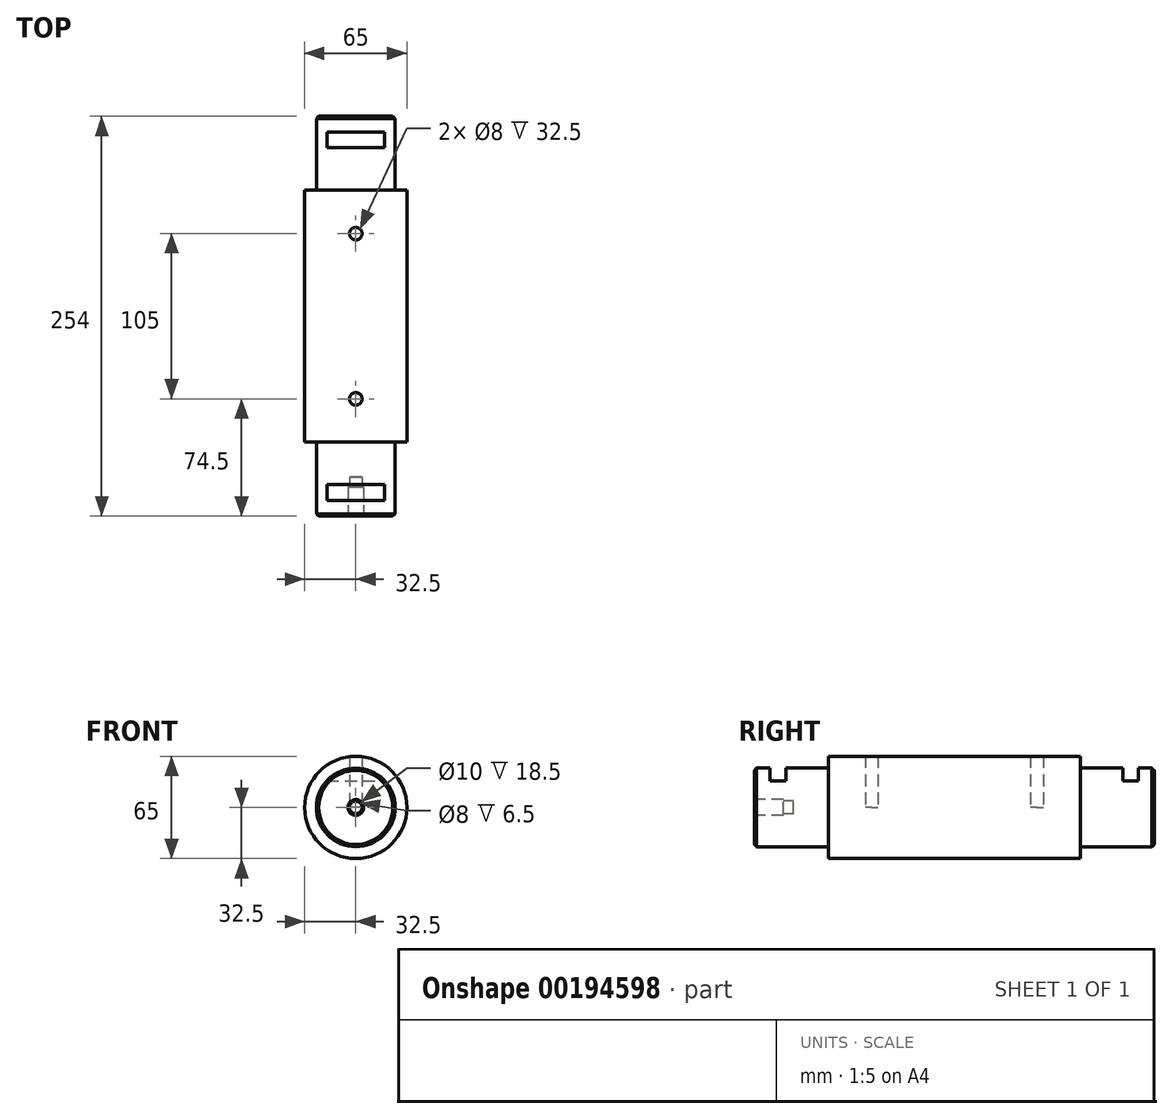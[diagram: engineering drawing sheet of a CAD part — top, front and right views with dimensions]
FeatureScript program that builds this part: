
annotation { "Feature Type Name" : "Feature", "Feature Type Description" : "" }
export const myFeature = defineFeature(function(context is Context, id is Id, definition is map)
    precondition{}
    {
        {
            var Q0;
            Q0=qCreatedBy(makeId("Front.planeOp"),FACE);
            var sketch = newSketch(context, id + "F0", { "sketchPlane" : qUnion([Q0])});
            skCircle(sketch, "E0", {"center": v(0, 0) * mm, "radius": 25 * mm});
            skSolve(sketch);
        }
        {
            var Q0;
            Q0 = qSketchRegion(id + "F0", true);
            extrude(context, id + "F1", {"entities" : qUnion([Q0]), "oppositeDirection" : true, "depth" : 47 * mm});
        }
        {
            var Q0;
            Q0=makeQuery(id+"F1.opExtrude","CAP_FACE",FACE,{"disambiguationData":[OSD([sQuery(id+"F0.wireOp",EDGE,"E0")])],"isStart":false});
            var sketch = newSketch(context, id + "F2", { "sketchPlane" : qUnion([Q0])});
            skCircle(sketch, "E1", {"center": v(0, 0) * mm, "radius": 32.5 * mm});
            skSolve(sketch);
        }
        {
            var Q0;
            Q0 = qSketchRegion(id + "F2", true);
            extrude(context, id + "F3", {"entities" : qUnion([Q0]), "operationType" : NewBodyOperationType.ADD, "depth" : 160 * mm});
        }
        {
            var Q0;
            Q0=makeQuery(id+"F3.opExtrude","CAP_FACE",FACE,{"disambiguationData":[OSD([sQuery(id+"F2.wireOp",EDGE,"E1")])],"isStart":false});
            var sketch = newSketch(context, id + "F4", { "sketchPlane" : qUnion([Q0])});
            skCircle(sketch, "E2", {"center": v(0, 0) * mm, "radius": 25 * mm});
            skSolve(sketch);
        }
        {
            var Q0;
            Q0 = qSketchRegion(id + "F4", true);
            extrude(context, id + "F5", {"entities" : qUnion([Q0]), "operationType" : NewBodyOperationType.ADD, "depth" : 47 * mm});
        }
        {
            var Q0;
            Q0=qCreatedBy(makeId("Top.planeOp"),FACE);
            cPlane(context, id + "F6", {"entities" : qUnion([Q0]), "cplaneType" : CPlaneType.OFFSET, "offset" : 17 * mm, "width" : 150 * mm, "height" : 150 * mm});
        }
        {
            var Q0;
            Q0=qCreatedBy(id+"F6.planeOp",FACE);
            var sketch = newSketch(context, id + "F7", { "sketchPlane" : qUnion([Q0])});
            skLineSegment(sketch, "E3.bottom", {"start": v(-21.44, 20) * mm, "end": v(39.15, 20) * mm});
            skLineSegment(sketch, "E3.top", {"start": v(-21.44, 10) * mm, "end": v(39.15, 10) * mm});
            skLineSegment(sketch, "E3.left", {"start": v(-21.44, 20) * mm, "end": v(-21.44, 10) * mm});
            skLineSegment(sketch, "E3.right", {"start": v(39.15, 20) * mm, "end": v(39.15, 10) * mm});
            skSolve(sketch);
        }
        {
            var Q0;
            Q0=makeQuery(id+"F7.imprint","IMPRINT",FACE,{"disambiguationData":[TD([[makeQuery(id+"F7.imprint","IMPRINT",EDGE,{"derivedFrom":sQuery(id+"F7.wireOp",EDGE,"E3.bottom")}),-1.0]])]});
            extrude(context, id + "F8", {"entities" : qUnion([Q0]), "operationType" : NewBodyOperationType.REMOVE, "depth" : 25 * mm});
        }
        {
            var Q0;
            Q0=qCreatedBy(id+"F6.planeOp",FACE);
            var sketch = newSketch(context, id + "F9", { "sketchPlane" : qUnion([Q0])});
            skLineSegment(sketch, "E4.bottom", {"start": v(-25.82, 234) * mm, "end": v(29.68, 234) * mm});
            skLineSegment(sketch, "E4.top", {"start": v(-25.82, 244) * mm, "end": v(29.68, 244) * mm});
            skLineSegment(sketch, "E4.left", {"start": v(-25.82, 234) * mm, "end": v(-25.82, 244) * mm});
            skLineSegment(sketch, "E4.right", {"start": v(29.68, 234) * mm, "end": v(29.68, 244) * mm});
            skSolve(sketch);
        }
        {
            var Q0;
            Q0 = qSketchRegion(id + "F9", true);
            extrude(context, id + "F10", {"entities" : qUnion([Q0]), "operationType" : NewBodyOperationType.REMOVE, "depth" : 25 * mm});
        }
        {
            var Q0;
            Q0=qCreatedBy(makeId("Front.planeOp"),FACE);
            var sketch = newSketch(context, id + "F11", { "sketchPlane" : qUnion([Q0])});
            skCircle(sketch, "E5", {"center": v(0, 0) * mm, "radius": 4 * mm});
            skSolve(sketch);
        }
        {
            var Q0;
            Q0 = qSketchRegion(id + "F11", true);
            extrude(context, id + "F12", {"entities" : qUnion([Q0]), "operationType" : NewBodyOperationType.REMOVE, "oppositeDirection" : true, "depth" : 25 * mm});
        }
        {
            var Q0;
            Q0=qCreatedBy(makeId("Top.planeOp"),FACE);
            var sketch = newSketch(context, id + "F13", { "sketchPlane" : qUnion([Q0])});
            skCircle(sketch, "E6", {"center": v(0, 74.5) * mm, "radius": 4 * mm});
            skCircle(sketch, "E7", {"center": v(0, 179.5) * mm, "radius": 4 * mm});
            skSolve(sketch);
        }
        {
            var Q0;
            Q0 = qSketchRegion(id + "F13", true);
            extrude(context, id + "F14", {"entities" : qUnion([Q0]), "operationType" : NewBodyOperationType.REMOVE, "depth" : 92 * mm});
        }
        {
            var Q0;
            Q0=qCreatedBy(makeId("Front.planeOp"),FACE);
            var sketch = newSketch(context, id + "F15", { "sketchPlane" : qUnion([Q0])});
            skCircle(sketch, "E8", {"center": v(0, 0) * mm, "radius": 5 * mm});
            skSolve(sketch);
        }
        {
            var Q0;
            Q0=makeQuery(id+"F15.imprint","IMPRINT",FACE,{"disambiguationData":[TD([[makeQuery(id+"F15.imprint","IMPRINT",EDGE,{"derivedFrom":sQuery(id+"F15.wireOp",EDGE,"E8")}),1.0]])]});
            extrude(context, id + "F16", {"entities" : qUnion([Q0]), "operationType" : NewBodyOperationType.REMOVE, "oppositeDirection" : true, "depth" : 18.5 * mm});
        }
        {
            var Q0;
            Q0=makeQuery(id+"F1.opExtrude","CAP_EDGE",EDGE,{"disambiguationData":[OSD([sQuery(id+"F0.wireOp",EDGE,"E0")])],"isStart":true});
            var Q1;
            Q1=makeQuery(id+"F5.opExtrude","CAP_EDGE",EDGE,{"disambiguationData":[OSD([sQuery(id+"F4.wireOp",EDGE,"E2")])],"isStart":false});
            chamfer(context, id + "F17", {"entities" : qUnion([Q0, Q1]), "width" : 1.5 * mm, "tangentPropagation" : true});
        }
    });
